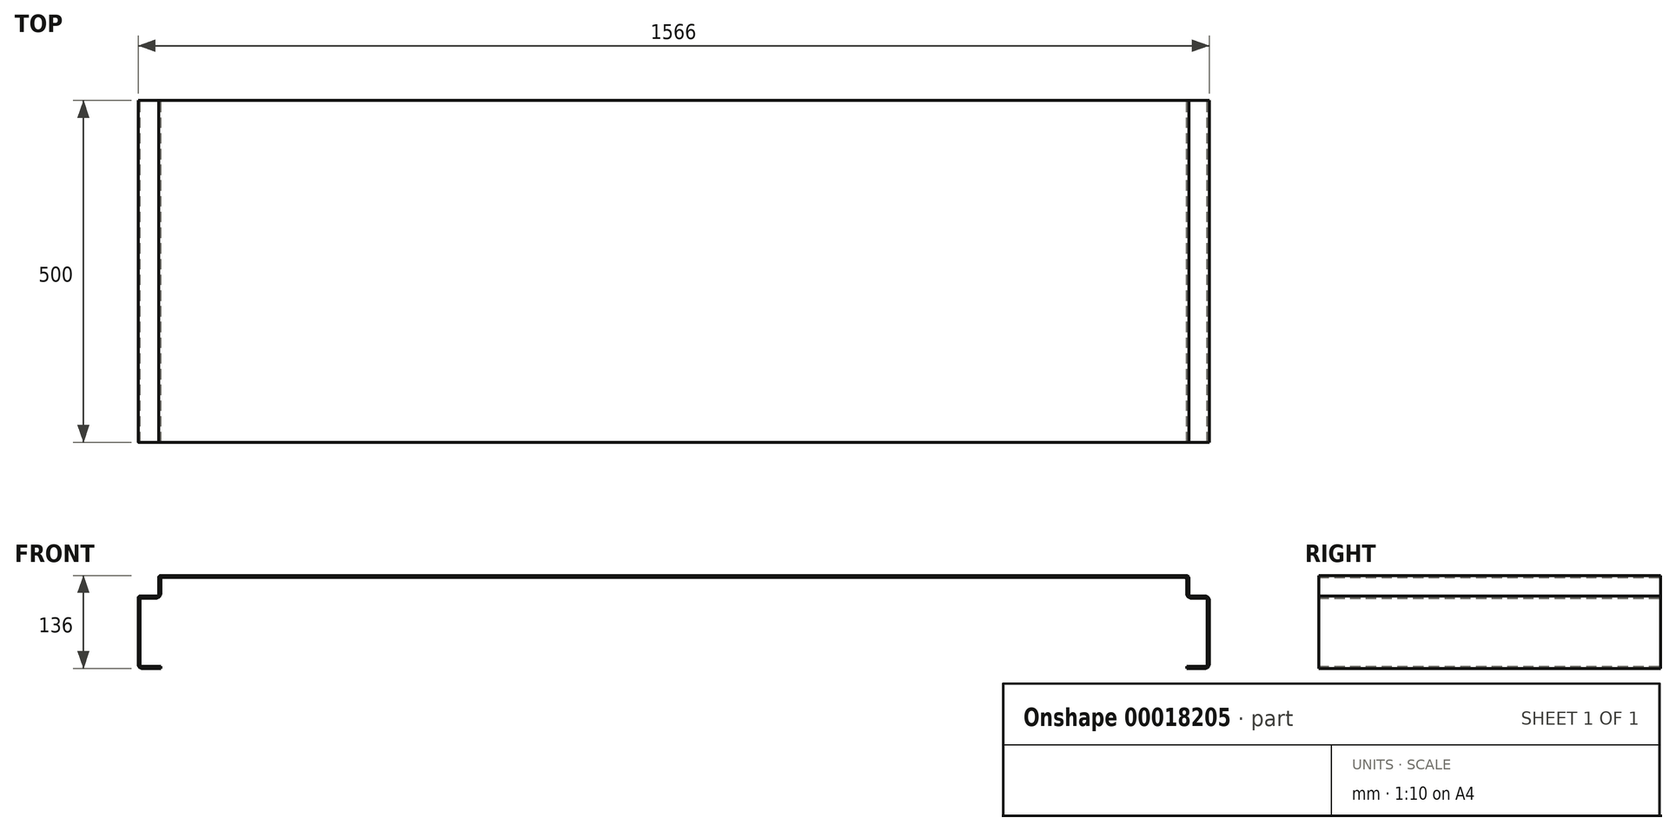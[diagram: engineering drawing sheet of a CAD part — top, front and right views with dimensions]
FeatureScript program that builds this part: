
annotation { "Feature Type Name" : "Feature", "Feature Type Description" : "" }
export const myFeature = defineFeature(function(context is Context, id is Id, definition is map)
    precondition{}
    {
        {
            var Q0;
            Q0=qCreatedBy(makeId("Front.planeOp"),FACE);
            var sketch = newSketch(context, id + "F0", { "sketchPlane" : qUnion([Q0])});
            skLineSegment(sketch, "E0", {"start": v(-138.88, 0) * mm, "end": v(-138.88, 100) * mm});
            skLineSegment(sketch, "E1", {"start": v(-138.88, 100) * mm, "end": v(-108.88, 100) * mm});
            skLineSegment(sketch, "E2", {"start": v(-108.88, 100) * mm, "end": v(-108.88, 130) * mm});
            skLineSegment(sketch, "E3", {"start": v(-108.88, 130) * mm, "end": v(1391.12, 130) * mm});
            skLineSegment(sketch, "E4", {"start": v(1391.12, 130) * mm, "end": v(1391.12, 100) * mm});
            skLineSegment(sketch, "E5", {"start": v(1391.12, 100) * mm, "end": v(1421.12, 100) * mm});
            skLineSegment(sketch, "E6", {"start": v(1421.12, 100) * mm, "end": v(1421.12, 0) * mm});
            skLineSegment(sketch, "E7", {"start": v(1421.12, 0) * mm, "end": v(1391.12, 0) * mm});
            skLineSegment(sketch, "E8", {"start": v(-138.88, 0) * mm, "end": v(-108.88, 0) * mm});
            skLineSegment(sketch, "E9.0", {"start": v(-135.68, -3) * mm, "end": v(-108.88, -3) * mm});
            skLineSegment(sketch, "E10.0", {"start": v(-141.88, 3.2) * mm, "end": v(-141.88, 103.2) * mm});
            skLineSegment(sketch, "E11.0", {"start": v(-135.68, 103) * mm, "end": v(-111.88, 103) * mm});
            skLineSegment(sketch, "E12.0", {"start": v(-111.88, 103) * mm, "end": v(-111.88, 130) * mm});
            skLineSegment(sketch, "E13.0", {"start": v(-105.68, 133) * mm, "end": v(1394.32, 133) * mm});
            skLineSegment(sketch, "E14.0", {"start": v(1394.12, 130) * mm, "end": v(1394.12, 103) * mm});
            skLineSegment(sketch, "E15.0", {"start": v(1394.32, 103) * mm, "end": v(1424.32, 103) * mm});
            skLineSegment(sketch, "E16.0", {"start": v(1424.12, 100) * mm, "end": v(1424.12, 0) * mm});
            skLineSegment(sketch, "E17.0", {"start": v(1424.12, -3) * mm, "end": v(1391, -3) * mm});
            skLineSegment(sketch, "E17.1", {"start": v(1424.12, 103) * mm, "end": v(1424.12, -3) * mm});
            skLineSegment(sketch, "E17.2", {"start": v(1394.12, 103) * mm, "end": v(1424.12, 103) * mm});
            skLineSegment(sketch, "E17.3", {"start": v(1394.12, 133) * mm, "end": v(1394.12, 103) * mm});
            skLineSegment(sketch, "E17.4", {"start": v(-111.88, 133) * mm, "end": v(1394.12, 133) * mm});
            skLineSegment(sketch, "E17.5", {"start": v(-111.88, 103) * mm, "end": v(-111.88, 133) * mm});
            skLineSegment(sketch, "E17.6", {"start": v(-141.88, 103) * mm, "end": v(-111.88, 103) * mm});
            skLineSegment(sketch, "E17.7", {"start": v(-141.88, -3) * mm, "end": v(-141.88, 103) * mm});
            skLineSegment(sketch, "E17.8", {"start": v(-141.88, -3) * mm, "end": v(-108.88, -3) * mm});
            skLineSegment(sketch, "E18", {"start": v(1391, -3) * mm, "end": v(1391.12, 0) * mm});
            skLineSegment(sketch, "E19", {"start": v(-108.88, 0) * mm, "end": v(-108.88, -3) * mm});
            skSolve(sketch);
        }
        {
            var Q0;
            Q0=makeQuery(id+"F0.imprint","IMPRINT",FACE,{"disambiguationData":[TD([[makeQuery(id+"F0.imprint","IMPRINT",EDGE,{"derivedFrom":sQuery(id+"F0.wireOp",EDGE,"E0")}),1.0]])]});
            extrude(context, id + "F1", {"entities" : qUnion([Q0]), "depth" : 500 * mm});
        }
        {
            var Q0;
            Q0=makeQuery(id+"F1.opExtrude","SWEPT_EDGE",EDGE,{"disambiguationData":[OSD([sQuery(id+"F0.wireOp",EDGE,"E17.5"),sQuery(id+"F0.wireOp",EDGE,"E17.6")])]});
            var Q1;
            Q1=makeQuery(id+"F1.opExtrude","SWEPT_EDGE",EDGE,{"disambiguationData":[OSD([sQuery(id+"F0.wireOp",EDGE,"E6"),sQuery(id+"F0.wireOp",EDGE,"E7")])]});
            var Q2;
            Q2=makeQuery(id+"F1.opExtrude","SWEPT_EDGE",EDGE,{"disambiguationData":[OSD([sQuery(id+"F0.wireOp",EDGE,"E17.2"),sQuery(id+"F0.wireOp",EDGE,"E17.3")])]});
            var Q3;
            Q3=makeQuery(id+"F1.opExtrude","SWEPT_EDGE",EDGE,{"disambiguationData":[OSD([sQuery(id+"F0.wireOp",EDGE,"E0"),sQuery(id+"F0.wireOp",EDGE,"E8")])]});
            var Q4;
            Q4=makeQuery(id+"F1.opExtrude","SWEPT_EDGE",EDGE,{"disambiguationData":[OSD([sQuery(id+"F0.wireOp",EDGE,"E0"),sQuery(id+"F0.wireOp",EDGE,"E1")])]});
            var Q5;
            Q5=makeQuery(id+"F1.opExtrude","SWEPT_EDGE",EDGE,{"disambiguationData":[OSD([sQuery(id+"F0.wireOp",EDGE,"E2"),sQuery(id+"F0.wireOp",EDGE,"E3")])]});
            var Q6;
            Q6=makeQuery(id+"F1.opExtrude","SWEPT_EDGE",EDGE,{"disambiguationData":[OSD([sQuery(id+"F0.wireOp",EDGE,"E3"),sQuery(id+"F0.wireOp",EDGE,"E4")])]});
            var Q7;
            Q7=makeQuery(id+"F1.opExtrude","SWEPT_EDGE",EDGE,{"disambiguationData":[OSD([sQuery(id+"F0.wireOp",EDGE,"E5"),sQuery(id+"F0.wireOp",EDGE,"E6")])]});
            fillet(context, id + "F2", {"entities" : qUnion([Q0, Q1, Q2, Q3, Q4, Q5, Q6, Q7]), "radius" : 3 * mm, "tangentPropagation" : true, "allowEdgeOverflow" : false});
        }
        {
            var Q0;
            Q0=makeQuery(id+"F1.opExtrude","SWEPT_EDGE",EDGE,{"disambiguationData":[OSD([sQuery(id+"F0.wireOp",EDGE,"E17.7"),sQuery(id+"F0.wireOp",EDGE,"E17.8")])]});
            var Q1;
            Q1=makeQuery(id+"F1.opExtrude","SWEPT_EDGE",EDGE,{"disambiguationData":[OSD([sQuery(id+"F0.wireOp",EDGE,"E17.6"),sQuery(id+"F0.wireOp",EDGE,"E17.7")])]});
            var Q2;
            Q2=makeQuery(id+"F1.opExtrude","SWEPT_EDGE",EDGE,{"disambiguationData":[OSD([sQuery(id+"F0.wireOp",EDGE,"E17.4"),sQuery(id+"F0.wireOp",EDGE,"E17.5")])]});
            var Q3;
            Q3=makeQuery(id+"F1.opExtrude","SWEPT_EDGE",EDGE,{"disambiguationData":[OSD([sQuery(id+"F0.wireOp",EDGE,"E17.0"),sQuery(id+"F0.wireOp",EDGE,"E17.1")])]});
            var Q4;
            Q4=makeQuery(id+"F1.opExtrude","SWEPT_EDGE",EDGE,{"disambiguationData":[OSD([sQuery(id+"F0.wireOp",EDGE,"E17.1"),sQuery(id+"F0.wireOp",EDGE,"E17.2")])]});
            var Q5;
            Q5=makeQuery(id+"F1.opExtrude","SWEPT_EDGE",EDGE,{"disambiguationData":[OSD([sQuery(id+"F0.wireOp",EDGE,"E17.3"),sQuery(id+"F0.wireOp",EDGE,"E17.4")])]});
            var Q6;
            Q6=makeQuery(id+"F1.opExtrude","SWEPT_EDGE",EDGE,{"disambiguationData":[OSD([sQuery(id+"F0.wireOp",EDGE,"E4"),sQuery(id+"F0.wireOp",EDGE,"E5")])]});
            var Q7;
            Q7=makeQuery(id+"F1.opExtrude","SWEPT_EDGE",EDGE,{"disambiguationData":[OSD([sQuery(id+"F0.wireOp",EDGE,"E1"),sQuery(id+"F0.wireOp",EDGE,"E2")])]});
            fillet(context, id + "F3", {"entities" : qUnion([Q0, Q1, Q2, Q3, Q4, Q5, Q6, Q7]), "radius" : 6 * mm, "tangentPropagation" : true, "allowEdgeOverflow" : false});
        }
    });
